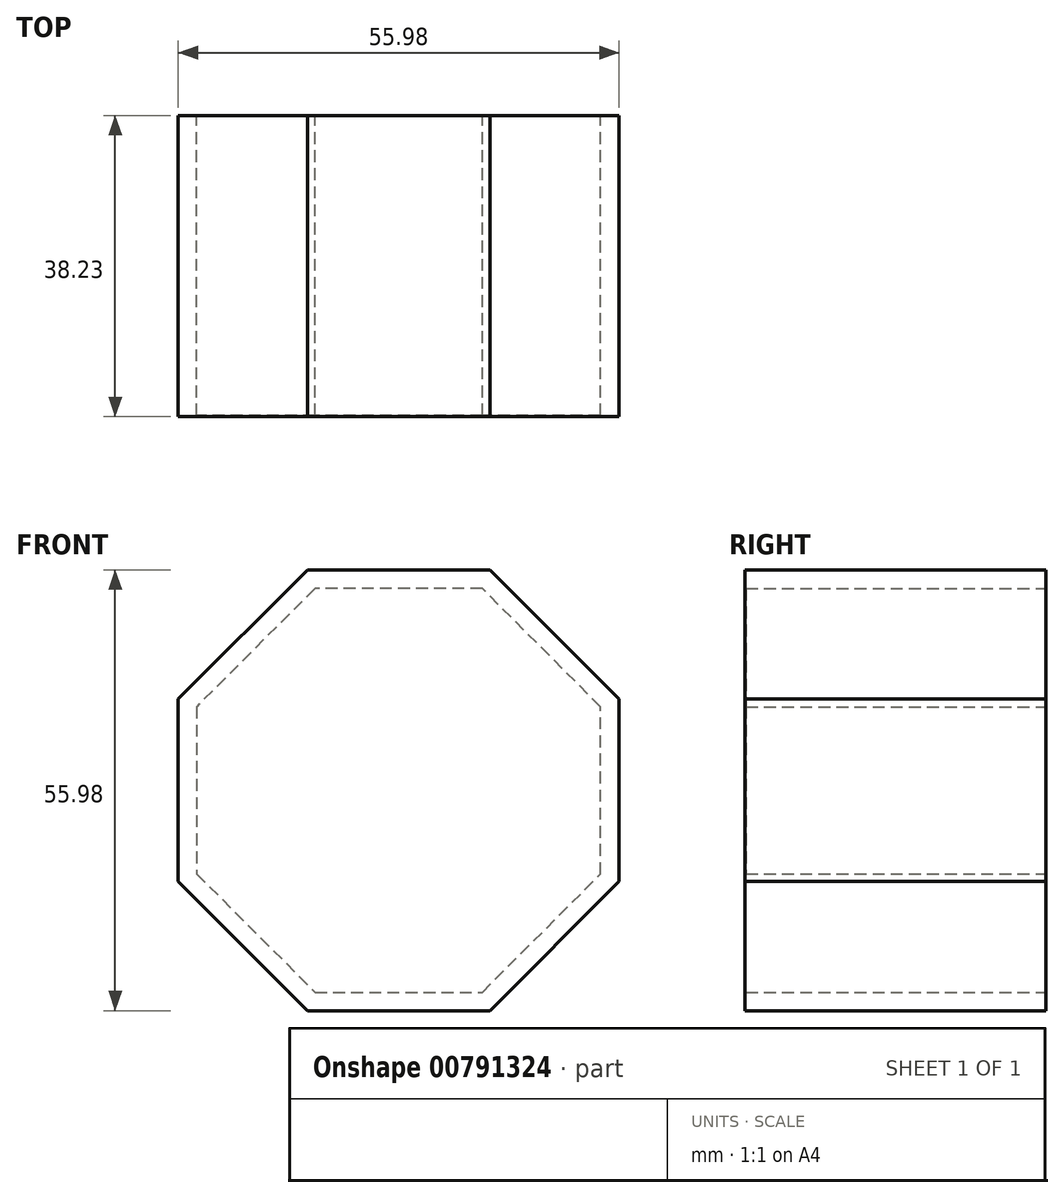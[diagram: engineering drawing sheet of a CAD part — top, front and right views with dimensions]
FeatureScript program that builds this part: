
annotation { "Feature Type Name" : "Feature", "Feature Type Description" : "" }
export const myFeature = defineFeature(function(context is Context, id is Id, definition is map)
    precondition{}
    {
        {
            var Q0;
            Q0=qCreatedBy(makeId("Front.planeOp"),FACE);
            var sketch = newSketch(context, id + "F0", { "sketchPlane" : qUnion([Q0])});
            skPoint(sketch, "E0", {"position": v(0, 28) * mm});
            skPoint(sketch, "E1", {"position": v(0, -28) * mm});
            skPoint(sketch, "E2", {"position": v(-28, 0) * mm});
            skPoint(sketch, "E3", {"position": v(28, 0) * mm});
            skLineSegment(sketch, "E4", {"start": v(0, 0) * mm, "end": v(-19.8, 19.8) * mm});
            skLineSegment(sketch, "E5", {"start": v(-19.8, -19.8) * mm, "end": v(0, 0) * mm});
            skLineSegment(sketch, "E6", {"start": v(19.8, 19.8) * mm, "end": v(0, 0) * mm});
            skLineSegment(sketch, "E7", {"start": v(19.8, -19.8) * mm, "end": v(0, 0) * mm});
            skLineSegment(sketch, "E8", {"start": v(0, 28) * mm, "end": v(0, 0) * mm, "construction": true});
            skPoint(sketch, "E9", {"position": v(-19.8, 19.8) * mm});
            skPoint(sketch, "E10", {"position": v(-19.8, -19.8) * mm});
            skPoint(sketch, "E11", {"position": v(19.8, -19.8) * mm});
            skPoint(sketch, "E12", {"position": v(19.8, 19.8) * mm});
            skLineSegment(sketch, "E13", {"start": v(28, 11.6) * mm, "end": v(28, -11.6) * mm});
            skLineSegment(sketch, "E14", {"start": v(-11.6, -28) * mm, "end": v(11.6, -28) * mm});
            skLineSegment(sketch, "E15", {"start": v(-28, 11.6) * mm, "end": v(-11.6, 28) * mm});
            skLineSegment(sketch, "E16", {"start": v(11.6, 28) * mm, "end": v(28, 11.6) * mm});
            skLineSegment(sketch, "E17", {"start": v(28, -11.6) * mm, "end": v(11.6, -28) * mm});
            skLineSegment(sketch, "E18", {"start": v(-28, -11.6) * mm, "end": v(-11.6, -28) * mm});
            skLineSegment(sketch, "E19.trimOffspring", {"start": v(-11.6, 28) * mm, "end": v(11.6, 28) * mm});
            skLineSegment(sketch, "E20.trimOffspring", {"start": v(-28, 11.6) * mm, "end": v(-28, -11.6) * mm});
            skPoint(sketch, "E21.start.orphan", {"position": v(-30.36, 28) * mm});
            skPoint(sketch, "E22.start.orphan", {"position": v(-28, 32.68) * mm});
            skPoint(sketch, "E23.orphan", {"position": v(-30.22, -28) * mm});
            skPoint(sketch, "E24.orphan", {"position": v(28, 34.59) * mm});
            skPoint(sketch, "E25.orphan", {"position": v(39.59, 0) * mm});
            skPoint(sketch, "E26", {"position": v(0, 0) * mm});
            skPoint(sketch, "E27", {"position": v(-28, 11.6) * mm});
            skPoint(sketch, "E28", {"position": v(-11.6, 28) * mm});
            skPoint(sketch, "E29", {"position": v(11.6, 28) * mm});
            skPoint(sketch, "E30", {"position": v(28, 11.6) * mm});
            skPoint(sketch, "E31", {"position": v(28, -11.6) * mm});
            skPoint(sketch, "E32", {"position": v(11.6, -28) * mm});
            skPoint(sketch, "E33", {"position": v(-11.6, -28) * mm});
            skPoint(sketch, "E34", {"position": v(-28, -11.6) * mm});
            skLineSegment(sketch, "E35", {"start": v(0, 0) * mm, "end": v(11.6, 28) * mm, "construction": true});
            skLineSegment(sketch, "E36", {"start": v(0, 0) * mm, "end": v(28, 11.6) * mm, "construction": true});
            skLineSegment(sketch, "E37", {"start": v(0, 0) * mm, "end": v(28, -11.6) * mm, "construction": true});
            skLineSegment(sketch, "E38", {"start": v(0, 0) * mm, "end": v(11.6, -28) * mm, "construction": true});
            skLineSegment(sketch, "E39", {"start": v(0, 0) * mm, "end": v(0, -28) * mm, "construction": true});
            skLineSegment(sketch, "E40.MirrorCS", {"start": v(0, 0) * mm, "end": v(-11.6, 28) * mm, "construction": true});
            skLineSegment(sketch, "E41.MirrorCS", {"start": v(0, 0) * mm, "end": v(-28, 11.6) * mm, "construction": true});
            skLineSegment(sketch, "E42.MirrorCS", {"start": v(0, 0) * mm, "end": v(-28, -11.6) * mm, "construction": true});
            skLineSegment(sketch, "E43.MirrorCS", {"start": v(0, 0) * mm, "end": v(-11.6, -28) * mm, "construction": true});
            skPoint(sketch, "E44", {"position": v(-25.65, 10.62) * mm});
            skLineSegment(sketch, "E45", {"start": v(-25.65, 10.62) * mm, "end": v(-25.65, -10.62) * mm});
            skLineSegment(sketch, "E46", {"start": v(-25.65, -10.62) * mm, "end": v(-10.62, -25.65) * mm});
            skLineSegment(sketch, "E47", {"start": v(-10.62, -25.65) * mm, "end": v(10.62, -25.65) * mm});
            skLineSegment(sketch, "E48", {"start": v(10.62, -25.65) * mm, "end": v(25.65, -10.62) * mm});
            skLineSegment(sketch, "E49", {"start": v(25.65, -10.62) * mm, "end": v(25.65, 10.62) * mm});
            skLineSegment(sketch, "E50", {"start": v(25.65, 10.62) * mm, "end": v(10.62, 25.65) * mm});
            skLineSegment(sketch, "E51", {"start": v(10.62, 25.65) * mm, "end": v(-10.62, 25.65) * mm});
            skLineSegment(sketch, "E52", {"start": v(-10.62, 25.65) * mm, "end": v(-25.65, 10.62) * mm});
            skSolve(sketch);
        }
        {
            var Q0;
            {var subQ3=sQuery(id+"F0.wireOp",EDGE,"E19.trimOffspring");Q0=makeQuery(id+"F0.imprint","IMPRINT",FACE,{"disambiguationData":[TD([[makeQuery(id+"F0.imprint","IMPRINT",EDGE,{"derivedFrom":subQ3}),-1.0]])]});}
            var Q1;
            {var subQ3=sQuery(id+"F0.wireOp",EDGE,"E20.trimOffspring");Q1=makeQuery(id+"F0.imprint","IMPRINT",FACE,{"disambiguationData":[TD([[makeQuery(id+"F0.imprint","IMPRINT",EDGE,{"derivedFrom":subQ3}),1.0]])]});}
            var Q2;
            {var subQ3=sQuery(id+"F0.wireOp",EDGE,"E13");Q2=makeQuery(id+"F0.imprint","IMPRINT",FACE,{"disambiguationData":[TD([[makeQuery(id+"F0.imprint","IMPRINT",EDGE,{"derivedFrom":subQ3}),-1.0]])]});}
            var Q3;
            {var subQ3=sQuery(id+"F0.wireOp",EDGE,"E14");Q3=makeQuery(id+"F0.imprint","IMPRINT",FACE,{"disambiguationData":[TD([[makeQuery(id+"F0.imprint","IMPRINT",EDGE,{"derivedFrom":subQ3}),1.0]])]});}
            extrude(context, id + "F1", {"entities" : qUnion([Q0, Q1, Q2, Q3]), "depth" : 38.1 * mm, "offsetDistance" : 25.4 * mm});
        }
        {
            var Q0;
            Q0=makeQuery(id+"F1.opExtrude","CAP_FACE",FACE,{"disambiguationData":[OSD([sQuery(id+"F0.wireOp",EDGE,"E13"),sQuery(id+"F0.wireOp",EDGE,"E14"),sQuery(id+"F0.wireOp",EDGE,"E15"),sQuery(id+"F0.wireOp",EDGE,"E16"),sQuery(id+"F0.wireOp",EDGE,"E17"),sQuery(id+"F0.wireOp",EDGE,"E18"),sQuery(id+"F0.wireOp",EDGE,"E19.trimOffspring"),sQuery(id+"F0.wireOp",EDGE,"E20.trimOffspring"),sQuery(id+"F0.wireOp",EDGE,"E45"),sQuery(id+"F0.wireOp",EDGE,"E46"),sQuery(id+"F0.wireOp",EDGE,"E47"),sQuery(id+"F0.wireOp",EDGE,"E48"),sQuery(id+"F0.wireOp",EDGE,"E49"),sQuery(id+"F0.wireOp",EDGE,"E50"),sQuery(id+"F0.wireOp",EDGE,"E51"),sQuery(id+"F0.wireOp",EDGE,"E52")])],"isStart":false});
            var sketch = newSketch(context, id + "F2", { "sketchPlane" : qUnion([Q0])});
            skLineSegment(sketch, "E53", {"start": v(-28, 11.6) * mm, "end": v(-11.6, 28) * mm});
            skLineSegment(sketch, "E54", {"start": v(-11.6, 28) * mm, "end": v(11.6, 28) * mm});
            skLineSegment(sketch, "E55", {"start": v(11.6, 28) * mm, "end": v(28, 11.6) * mm});
            skLineSegment(sketch, "E56", {"start": v(28, 11.6) * mm, "end": v(28, -11.6) * mm});
            skLineSegment(sketch, "E57", {"start": v(28, -11.6) * mm, "end": v(11.6, -28) * mm});
            skLineSegment(sketch, "E58", {"start": v(11.6, -28) * mm, "end": v(-11.6, -28) * mm});
            skLineSegment(sketch, "E59", {"start": v(-11.6, -28) * mm, "end": v(-28, -11.6) * mm});
            skLineSegment(sketch, "E60", {"start": v(-28, -11.6) * mm, "end": v(-28, 11.6) * mm});
            skSolve(sketch);
        }
        {
            var Q0;
            Q0 = qSketchRegion(id + "F2", true);
            extrude(context, id + "F3", {"entities" : qUnion([Q0]), "operationType" : NewBodyOperationType.ADD, "depth" : 0.13 * mm, "offsetDistance" : 25.4 * mm});
        }
    });
